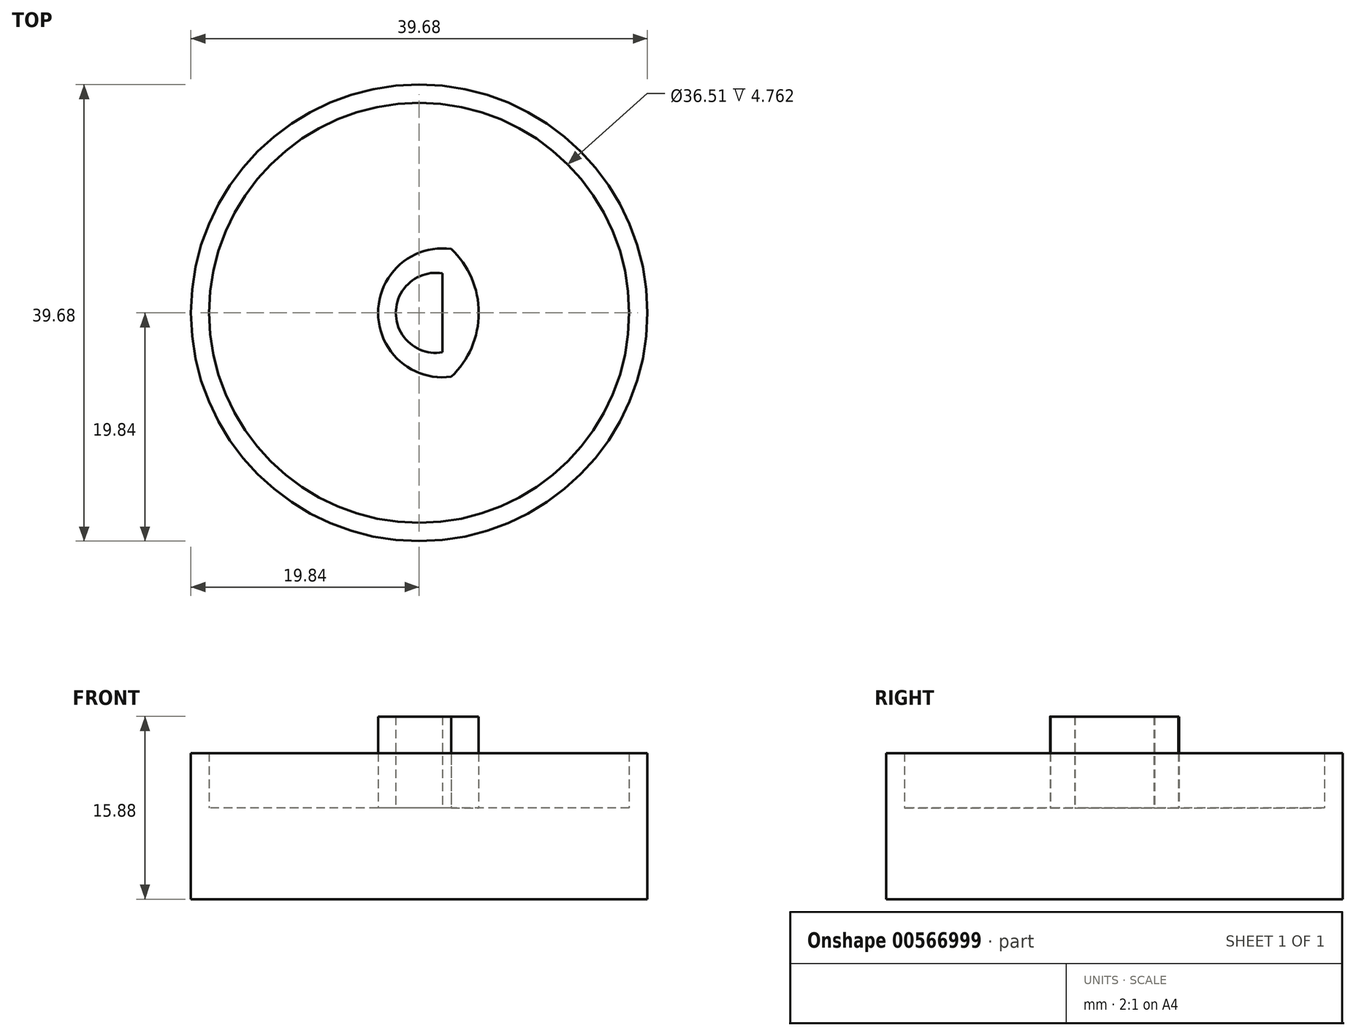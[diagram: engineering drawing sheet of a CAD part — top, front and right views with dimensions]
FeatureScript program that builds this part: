
annotation { "Feature Type Name" : "Feature", "Feature Type Description" : "" }
export const myFeature = defineFeature(function(context is Context, id is Id, definition is map)
    precondition{}
    {
        {
            var Q0;
            Q0=qCreatedBy(makeId("Top.planeOp"),FACE);
            var sketch = newSketch(context, id + "F0", { "sketchPlane" : qUnion([Q0])});
            skCircle(sketch, "E0", {"center": v(0, 0) * mm, "radius": 19.84 * mm});
            skSolve(sketch);
        }
        {
            var Q0;
            Q0 = qSketchRegion(id + "F0", true);
            extrude(context, id + "F1", {"entities" : qUnion([Q0]), "depth" : 6.35 * mm, "offsetDistance" : 25.4 * mm});
        }
        {
            var Q0;
            Q0=makeQuery(id+"F1.opExtrude","CAP_FACE",FACE,{"disambiguationData":[OSD([sQuery(id+"F0.wireOp",EDGE,"E0")])],"isStart":false});
            shell(context, id + "F2", {"entities" : qUnion([Q0]), "thickness" : 1.59 * mm});
        }
        {
            var Q0;
            {var subQ0=sQuery(id+"F0.wireOp",EDGE,"E0");Q0=makeQuery(id+"F2.opShell","OFFSET_FACE",FACE,{"disambiguationData":[OSD([subQ0]),TDD([makeQuery(id+"F1.opExtrude","CAP_FACE",FACE,{"disambiguationData":[OSD([subQ0])],"isStart":true})])]});}
            var sketch = newSketch(context, id + "F3", { "sketchPlane" : qUnion([Q0])});
            skLineSegment(sketch, "E1", {"start": v(2.03, -3.43) * mm, "end": v(2.03, 3.43) * mm});
            skArc(sketch, "E2", {"start": v(2.03, 3.43) * mm, "mid": v(-2.03, 0) * mm, "end": v(2.03, -3.43) * mm});
            skPoint(sketch, "E3", {"position": v(2.03, 0) * mm});
            skPoint(sketch, "E4", {"position": v(-2.03, 0) * mm});
            skLineSegment(sketch, "E5", {"start": v(2.78, 5.56) * mm, "end": v(2.78, -5.56) * mm});
            skArc(sketch, "E6", {"start": v(2.78, 5.56) * mm, "mid": v(-3.57, 0) * mm, "end": v(2.78, -5.56) * mm});
            skPoint(sketch, "E7", {"position": v(-3.57, 0) * mm});
            skArc(sketch, "E8", {"start": v(2.78, -5.56) * mm, "mid": v(5.18, 0) * mm, "end": v(2.78, 5.56) * mm});
            skSolve(sketch);
        }
        {
            var Q0;
            Q0 = qSketchRegion(id + "F3", true);
            extrude(context, id + "F4", {"entities" : qUnion([Q0]), "operationType" : NewBodyOperationType.ADD, "depth" : 7.94 * mm, "offsetDistance" : 25.4 * mm});
        }
        {
            var Q0;
            Q0=makeQuery(id+"F1.opExtrude","CAP_FACE",FACE,{"disambiguationData":[OSD([sQuery(id+"F0.wireOp",EDGE,"E0")])],"isStart":true});
            var sketch = newSketch(context, id + "F5", { "sketchPlane" : qUnion([Q0])});
            skSolve(sketch);
        }
        {
            var Q0;
            Q0=makeQuery(id+"F5.imprint","IMPRINT",FACE,{"disambiguationData":[TD([[makeQuery(id+"F5.imprint","IMPRINT",EDGE,{"derivedFrom":makeQuery(id+"F1.opExtrude","CAP_EDGE",EDGE,{"disambiguationData":[OSD([sQuery(id+"F0.wireOp",EDGE,"E0")])],"isStart":true})}),-1.0]])]});
            var sketch = newSketch(context, id + "F6", { "sketchPlane" : qUnion([Q0])});
            skCircle(sketch, "E9", {"center": v(0, 0) * mm, "radius": 19.84 * mm});
            skSolve(sketch);
        }
        {
            var Q0;
            Q0 = qSketchRegion(id + "F6", true);
            extrude(context, id + "F7", {"entities" : qUnion([Q0]), "operationType" : NewBodyOperationType.ADD, "depth" : 6.35 * mm, "offsetDistance" : 25.4 * mm});
        }
    });
